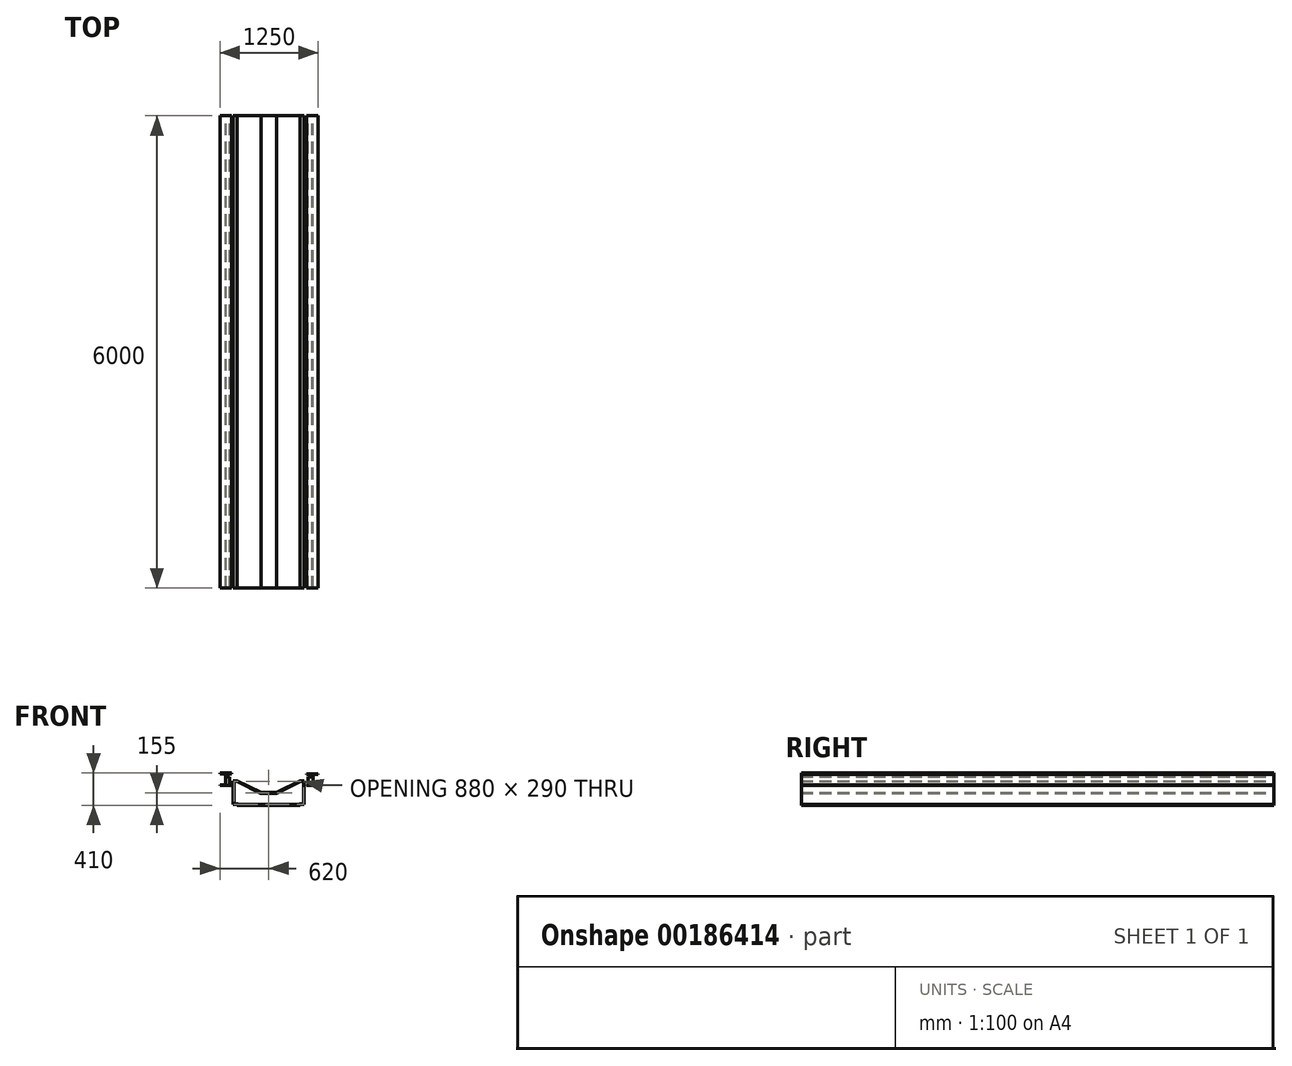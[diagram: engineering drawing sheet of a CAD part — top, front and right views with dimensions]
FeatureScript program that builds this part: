
annotation { "Feature Type Name" : "Feature", "Feature Type Description" : "" }
export const myFeature = defineFeature(function(context is Context, id is Id, definition is map)
    precondition{}
    {
        {
            var Q0;
            Q0=qCreatedBy(makeId("Front.planeOp"),FACE);
            var sketch = newSketch(context, id + "F0", { "sketchPlane" : qUnion([Q0])});
            skLineSegment(sketch, "E0.bottom", {"start": v(25, 50) * mm, "end": v(-25, 50) * mm});
            skLineSegment(sketch, "E0.top", {"start": v(25, -50) * mm, "end": v(-25, -50) * mm});
            skLineSegment(sketch, "E0.left", {"start": v(25, 50) * mm, "end": v(25, -50) * mm});
            skLineSegment(sketch, "E0.right", {"start": v(-25, 50) * mm, "end": v(-25, -50) * mm});
            skPoint(sketch, "E0.middle", {"position": v(0, 0) * mm});
            skLineSegment(sketch, "E1.bottom", {"start": v(1075, 50) * mm, "end": v(1025, 50) * mm});
            skLineSegment(sketch, "E1.top", {"start": v(1075, -50) * mm, "end": v(1025, -50) * mm});
            skLineSegment(sketch, "E1.left", {"start": v(1075, 50) * mm, "end": v(1075, -50) * mm});
            skLineSegment(sketch, "E1.right", {"start": v(1025, 50) * mm, "end": v(1025, -50) * mm});
            skPoint(sketch, "E1.middle", {"position": v(1050, 0) * mm});
            skPoint(sketch, "E2.firstSnap0", {"position": v(25, 0) * mm});
            skLineSegment(sketch, "E2.left", {"start": v(75, 0) * mm, "end": v(75, -300) * mm});
            skLineSegment(sketch, "E2.right", {"start": v(975, 0) * mm, "end": v(975, -300) * mm});
            skLineSegment(sketch, "E3.bottom", {"start": v(75, 0) * mm, "end": v(125, 0) * mm});
            skLineSegment(sketch, "E3.top", {"start": v(75, -300) * mm, "end": v(125, -300) * mm});
            skLineSegment(sketch, "E3.right", {"start": v(125, 0) * mm, "end": v(125, -300) * mm});
            skLineSegment(sketch, "E4.bottom", {"start": v(975, -300) * mm, "end": v(925, -300) * mm});
            skLineSegment(sketch, "E4.top", {"start": v(975, 0) * mm, "end": v(925, 0) * mm});
            skLineSegment(sketch, "E4.left", {"start": v(975, -300) * mm, "end": v(975, 0) * mm});
            skLineSegment(sketch, "E4.right", {"start": v(925, -300) * mm, "end": v(925, 0) * mm});
            skLineSegment(sketch, "E5", {"start": v(125, 0) * mm, "end": v(425, -150) * mm});
            skPoint(sketch, "E5.endSnap0", {"position": v(125, -150) * mm});
            skLineSegment(sketch, "E6", {"start": v(425, -150) * mm, "end": v(625, -150) * mm});
            skLineSegment(sketch, "E7", {"start": v(625, -150) * mm, "end": v(925, 0) * mm});
            skLineSegment(sketch, "E8", {"start": v(125, -10) * mm, "end": v(425, -160) * mm});
            skLineSegment(sketch, "E9", {"start": v(425, -160) * mm, "end": v(625, -160) * mm});
            skLineSegment(sketch, "E10", {"start": v(625, -160) * mm, "end": v(925, -10) * mm});
            skLineSegment(sketch, "E11", {"start": v(125, -300) * mm, "end": v(925, -300) * mm});
            skLineSegment(sketch, "E12", {"start": v(925, -310) * mm, "end": v(125, -310) * mm});
            skLineSegment(sketch, "E13", {"start": v(125, -310) * mm, "end": v(125, -300) * mm});
            skLineSegment(sketch, "E14", {"start": v(925, -310) * mm, "end": v(925, -300) * mm});
            skLineSegment(sketch, "E15", {"start": v(1075, -50) * mm, "end": v(1005, -50) * mm});
            skLineSegment(sketch, "E16", {"start": v(1005, -50) * mm, "end": v(1005, -60) * mm});
            skLineSegment(sketch, "E17", {"start": v(1005, -60) * mm, "end": v(1155, -60) * mm});
            skLineSegment(sketch, "E18", {"start": v(1155, -60) * mm, "end": v(1155, -50) * mm});
            skLineSegment(sketch, "E19", {"start": v(1155, -50) * mm, "end": v(1085, -50) * mm});
            skLineSegment(sketch, "E20", {"start": v(1085, -50) * mm, "end": v(1085, 80) * mm});
            skLineSegment(sketch, "E21", {"start": v(1085, 80) * mm, "end": v(1155, 80) * mm});
            skLineSegment(sketch, "E22", {"start": v(1155, 80) * mm, "end": v(1155, 90) * mm});
            skLineSegment(sketch, "E23", {"start": v(1155, 90) * mm, "end": v(1005, 90) * mm});
            skLineSegment(sketch, "E24", {"start": v(1005, 90) * mm, "end": v(1005, 80) * mm});
            skLineSegment(sketch, "E25", {"start": v(1005, 80) * mm, "end": v(1075, 80) * mm});
            skLineSegment(sketch, "E26", {"start": v(1075, 80) * mm, "end": v(1075, -50) * mm});
            skLineSegment(sketch, "E27", {"start": v(-25, -50) * mm, "end": v(55, -50) * mm});
            skPoint(sketch, "E27.endSnap0", {"position": v(0, -50) * mm});
            skLineSegment(sketch, "E28", {"start": v(55, -50) * mm, "end": v(55, -60) * mm});
            skLineSegment(sketch, "E29", {"start": v(55, -60) * mm, "end": v(-95, -60) * mm});
            skLineSegment(sketch, "E30", {"start": v(-95, -60) * mm, "end": v(-95, -50) * mm});
            skLineSegment(sketch, "E31", {"start": v(-95, -50) * mm, "end": v(-15, -50) * mm});
            skLineSegment(sketch, "E32", {"start": v(-15, -50) * mm, "end": v(-15, 90) * mm});
            skLineSegment(sketch, "E33", {"start": v(-15, 90) * mm, "end": v(-95, 90) * mm});
            skLineSegment(sketch, "E34", {"start": v(-95, 90) * mm, "end": v(-95, 100) * mm});
            skLineSegment(sketch, "E35", {"start": v(-95, 100) * mm, "end": v(55, 100) * mm});
            skLineSegment(sketch, "E36", {"start": v(55, 100) * mm, "end": v(55, 90) * mm});
            skLineSegment(sketch, "E37", {"start": v(55, 90) * mm, "end": v(-25, 90) * mm});
            skLineSegment(sketch, "E38", {"start": v(-25, 90) * mm, "end": v(-25, -50) * mm});
            skSolve(sketch);
        }
        {
            var Q0;
            Q0 = qSketchRegion(id + "F0", true);
            extrude(context, id + "F1", {"entities" : qUnion([Q0]), "depth" : 6000 * mm});
        }
        {
            var Q0;
            Q0=makeQuery(id+"F1.opExtrude","CAP_FACE",FACE,{"disambiguationData":[OSD([sQuery(id+"F0.wireOp",EDGE,"E3.bottom"),sQuery(id+"F0.wireOp",EDGE,"E3.top"),sQuery(id+"F0.wireOp",EDGE,"E2.left"),sQuery(id+"F0.wireOp",EDGE,"E4.bottom"),sQuery(id+"F0.wireOp",EDGE,"E4.top"),sQuery(id+"F0.wireOp",EDGE,"E4.left"),sQuery(id+"F0.wireOp",EDGE,"E5"),sQuery(id+"F0.wireOp",EDGE,"E6"),sQuery(id+"F0.wireOp",EDGE,"E7"),sQuery(id+"F0.wireOp",EDGE,"E12"),sQuery(id+"F0.wireOp",EDGE,"E13"),sQuery(id+"F0.wireOp",EDGE,"E14")])],"isStart":true});
            var Q1;
            Q1=makeQuery(id+"F1.opExtrude","CAP_FACE",FACE,{"disambiguationData":[OSD([sQuery(id+"F0.wireOp",EDGE,"E3.bottom"),sQuery(id+"F0.wireOp",EDGE,"E3.top"),sQuery(id+"F0.wireOp",EDGE,"E2.left"),sQuery(id+"F0.wireOp",EDGE,"E4.bottom"),sQuery(id+"F0.wireOp",EDGE,"E4.top"),sQuery(id+"F0.wireOp",EDGE,"E4.left"),sQuery(id+"F0.wireOp",EDGE,"E5"),sQuery(id+"F0.wireOp",EDGE,"E6"),sQuery(id+"F0.wireOp",EDGE,"E7"),sQuery(id+"F0.wireOp",EDGE,"E12"),sQuery(id+"F0.wireOp",EDGE,"E13"),sQuery(id+"F0.wireOp",EDGE,"E14")])],"isStart":false});
            shell(context, id + "F2", {"entities" : qUnion([Q0, Q1]), "thickness" : 10 * mm});
        }
    });
